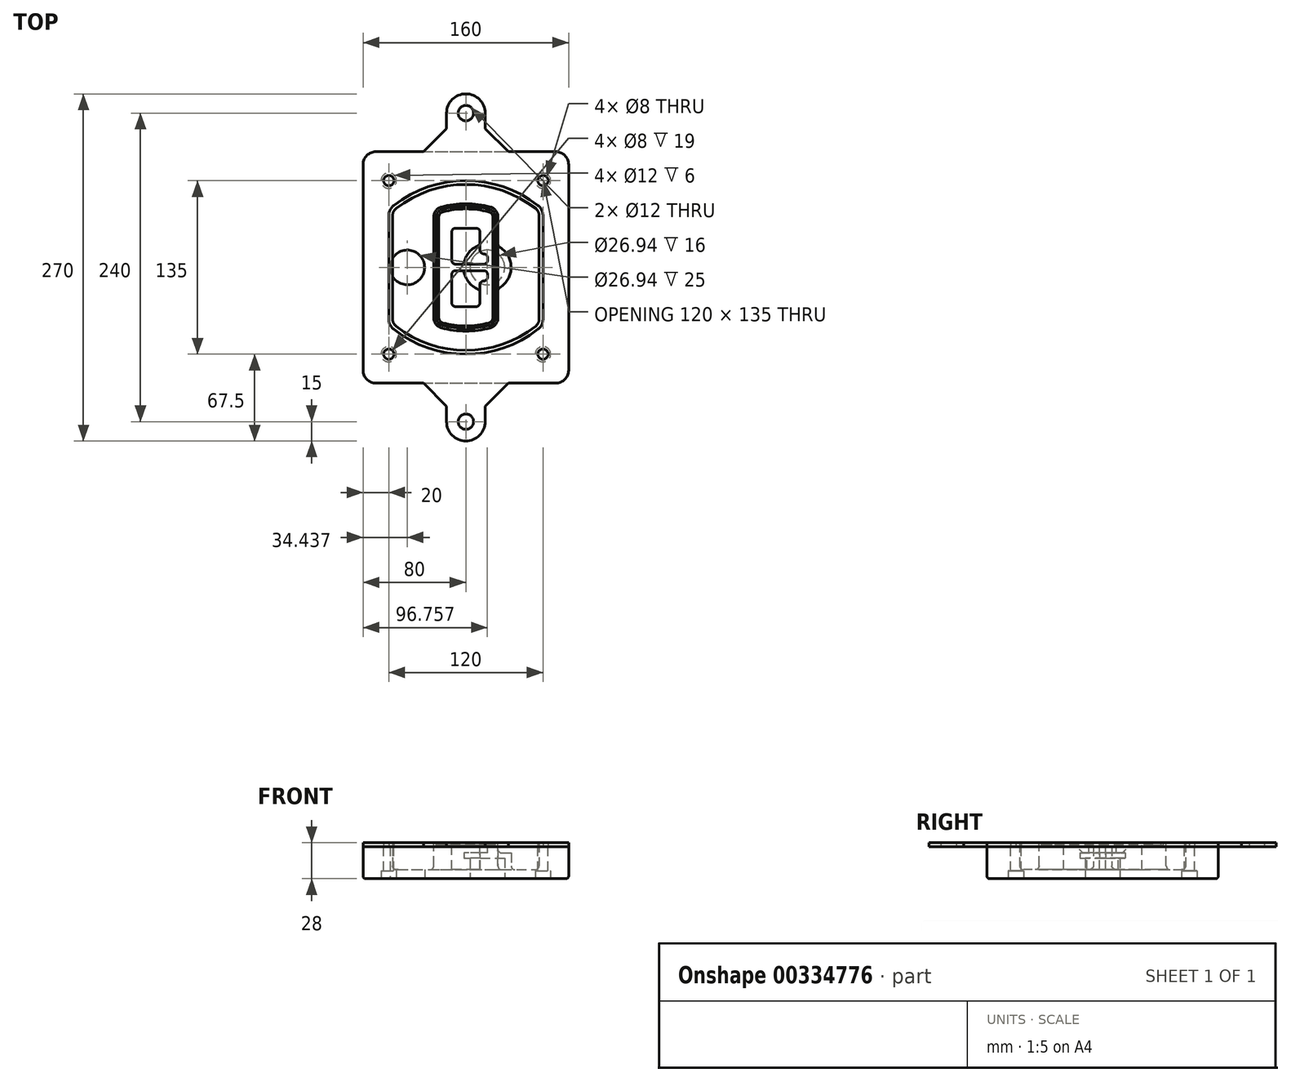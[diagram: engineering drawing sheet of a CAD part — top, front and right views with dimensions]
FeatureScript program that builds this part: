
annotation { "Feature Type Name" : "Feature", "Feature Type Description" : "" }
export const myFeature = defineFeature(function(context is Context, id is Id, definition is map)
    precondition{}
    {
        {
            var Q0;
            Q0=qCreatedBy(makeId("Top.planeOp"),FACE);
            var sketch = newSketch(context, id + "F0", { "sketchPlane" : qUnion([Q0])});
            skPoint(sketch, "E0.rect.middle", {"position": v(0, 0) * mm});
            skLineSegment(sketch, "E1.bottom", {"start": v(-70, -90) * mm, "end": v(70, -90) * mm});
            skLineSegment(sketch, "E1.top", {"start": v(-70, 90) * mm, "end": v(70, 90) * mm});
            skLineSegment(sketch, "E1.left", {"start": v(-80, -80) * mm, "end": v(-80, 80) * mm});
            skLineSegment(sketch, "E1.right", {"start": v(80, -80) * mm, "end": v(80, 80) * mm});
            skLineSegment(sketch, "E2", {"start": v(-80, 90) * mm, "end": v(80, -90) * mm, "construction": true});
            skLineSegment(sketch, "E3", {"start": v(80, 90) * mm, "end": v(-80, -90) * mm, "construction": true});
            skCircle(sketch, "E4", {"center": v(-60, 67.5) * mm, "radius": 4 * mm});
            skCircle(sketch, "E5", {"center": v(60, 67.5) * mm, "radius": 4 * mm});
            skCircle(sketch, "E6", {"center": v(60, -67.5) * mm, "radius": 4 * mm});
            skCircle(sketch, "E7", {"center": v(-60, -67.5) * mm, "radius": 4 * mm});
            skLineSegment(sketch, "E8", {"start": v(-60, 67.5) * mm, "end": v(60, 67.5) * mm, "construction": true});
            skLineSegment(sketch, "E9", {"start": v(60, 67.5) * mm, "end": v(60, -67.5) * mm, "construction": true});
            skLineSegment(sketch, "E10", {"start": v(60, -67.5) * mm, "end": v(-60, -67.5) * mm, "construction": true});
            skLineSegment(sketch, "E11", {"start": v(-60, -67.5) * mm, "end": v(-60, 67.5) * mm, "construction": true});
            skLineSegment(sketch, "E12", {"start": v(-60, 40.3) * mm, "end": v(-60, -40.3) * mm});
            skLineSegment(sketch, "E13", {"start": v(60, 40.3) * mm, "end": v(60, -40.3) * mm});
            skArc(sketch, "E14", {"start": v(56.15, 48.18) * mm, "mid": v(0, 67.5) * mm, "end": v(-56.15, 48.18) * mm});
            skArc(sketch, "E15", {"start": v(-56.15, -48.18) * mm, "mid": v(0, -67.5) * mm, "end": v(56.15, -48.18) * mm});
            skLineSegment(sketch, "E16", {"start": v(-60, 0) * mm, "end": v(60, 0) * mm, "construction": true});
            skPoint(sketch, "E17.visualSharp", {"position": v(-60, -45) * mm});
            skArc(sketch, "E17.filletArc", {"start": v(-60, -40.3) * mm, "mid": v(-58.99, -44.68) * mm, "end": v(-56.15, -48.18) * mm});
            skPoint(sketch, "E18.visualSharp", {"position": v(-60, 45) * mm});
            skArc(sketch, "E18.filletArc", {"start": v(-56.15, 48.18) * mm, "mid": v(-58.99, 44.68) * mm, "end": v(-60, 40.3) * mm});
            skPoint(sketch, "E19.visualSharp", {"position": v(60, 45) * mm});
            skArc(sketch, "E19.filletArc", {"start": v(60, 40.3) * mm, "mid": v(58.99, 44.68) * mm, "end": v(56.15, 48.18) * mm});
            skPoint(sketch, "E20.visualSharp", {"position": v(60, -45) * mm});
            skArc(sketch, "E20.filletArc", {"start": v(56.15, -48.18) * mm, "mid": v(58.99, -44.68) * mm, "end": v(60, -40.3) * mm});
            skPoint(sketch, "E21.visualSharp", {"position": v(-80, 90) * mm});
            skArc(sketch, "E21.filletArc", {"start": v(-70, 90) * mm, "mid": v(-77.07, 87.07) * mm, "end": v(-80, 80) * mm});
            skPoint(sketch, "E22.visualSharp", {"position": v(80, 90) * mm});
            skArc(sketch, "E22.filletArc", {"start": v(80, 80) * mm, "mid": v(77.07, 87.07) * mm, "end": v(70, 90) * mm});
            skPoint(sketch, "E23.visualSharp", {"position": v(80, -90) * mm});
            skArc(sketch, "E23.filletArc", {"start": v(70, -90) * mm, "mid": v(77.07, -87.07) * mm, "end": v(80, -80) * mm});
            skPoint(sketch, "E24.visualSharp", {"position": v(-80, -90) * mm});
            skArc(sketch, "E24.filletArc", {"start": v(-80, -80) * mm, "mid": v(-77.07, -87.07) * mm, "end": v(-70, -90) * mm});
            skArc(sketch, "E25.0", {"start": v(57, 40.3) * mm, "mid": v(56.3, 43.36) * mm, "end": v(54.3, 45.81) * mm});
            skLineSegment(sketch, "E25.1", {"start": v(57, 40.3) * mm, "end": v(57, -40.3) * mm});
            skArc(sketch, "E25.2", {"start": v(54.3, -45.81) * mm, "mid": v(56.3, -43.36) * mm, "end": v(57, -40.3) * mm});
            skArc(sketch, "E25.3", {"start": v(-54.3, -45.81) * mm, "mid": v(0, -64.5) * mm, "end": v(54.3, -45.81) * mm});
            skArc(sketch, "E25.4", {"start": v(-57, -40.3) * mm, "mid": v(-56.3, -43.36) * mm, "end": v(-54.3, -45.81) * mm});
            skArc(sketch, "E25.5", {"start": v(54.3, 45.81) * mm, "mid": v(0, 64.5) * mm, "end": v(-54.3, 45.81) * mm});
            skLineSegment(sketch, "E25.6", {"start": v(-57, 40.3) * mm, "end": v(-57, -40.3) * mm});
            skArc(sketch, "E25.7", {"start": v(-54.3, 45.81) * mm, "mid": v(-56.3, 43.36) * mm, "end": v(-57, 40.3) * mm});
            skArc(sketch, "E26.0", {"start": v(-58.62, 51.33) * mm, "mid": v(-62.58, 46.43) * mm, "end": v(-64, 40.3) * mm});
            skArc(sketch, "E26.1", {"start": v(58.62, 51.33) * mm, "mid": v(0, 71.5) * mm, "end": v(-58.62, 51.33) * mm});
            skArc(sketch, "E26.2", {"start": v(64, 40.3) * mm, "mid": v(62.58, 46.43) * mm, "end": v(58.62, 51.33) * mm});
            skLineSegment(sketch, "E26.3", {"start": v(64, 40.3) * mm, "end": v(64, -40.3) * mm});
            skArc(sketch, "E26.4", {"start": v(58.62, -51.33) * mm, "mid": v(62.58, -46.43) * mm, "end": v(64, -40.3) * mm});
            skLineSegment(sketch, "E26.5", {"start": v(-64, 40.3) * mm, "end": v(-64, -40.3) * mm});
            skArc(sketch, "E26.6", {"start": v(-58.62, -51.33) * mm, "mid": v(0, -71.5) * mm, "end": v(58.62, -51.33) * mm});
            skArc(sketch, "E26.7", {"start": v(-64, -40.3) * mm, "mid": v(-62.58, -46.43) * mm, "end": v(-58.62, -51.33) * mm});
            skSolve(sketch);
        }
        {
            var Q0;
            Q0=makeQuery(id+"F0.imprint","IMPRINT",FACE,{"disambiguationData":[TD([[makeQuery(id+"F0.imprint","IMPRINT",EDGE,{"derivedFrom":sQuery(id+"F0.wireOp",EDGE,"E1.bottom")}),1.0]])]});
            var Q1;
            Q1=makeQuery(id+"F0.imprint","IMPRINT",FACE,{"disambiguationData":[TD([[makeQuery(id+"F0.imprint","IMPRINT",EDGE,{"derivedFrom":sQuery(id+"F0.wireOp",EDGE,"E12")}),1.0]])]});
            var Q2;
            Q2=makeQuery(id+"F0.imprint","IMPRINT",FACE,{"disambiguationData":[TD([[makeQuery(id+"F0.imprint","IMPRINT",EDGE,{"derivedFrom":sQuery(id+"F0.wireOp",EDGE,"E25.0")}),1.0]])]});
            var Q3;
            Q3=makeQuery(id+"F0.imprint","IMPRINT",FACE,{"disambiguationData":[TD([[makeQuery(id+"F0.imprint","IMPRINT",EDGE,{"derivedFrom":sQuery(id+"F0.wireOp",EDGE,"E12")}),-1.0]])]});
            extrude(context, id + "F1", {"entities" : qUnion([Q0, Q1, Q2, Q3]), "oppositeDirection" : true, "depth" : 25 * mm});
        }
        {
            var Q0;
            Q0=makeQuery(id+"F0.imprint","IMPRINT",FACE,{"disambiguationData":[TD([[makeQuery(id+"F0.imprint","IMPRINT",EDGE,{"derivedFrom":sQuery(id+"F0.wireOp",EDGE,"E12")}),1.0]])]});
            extrude(context, id + "F2", {"entities" : qUnion([Q0]), "operationType" : NewBodyOperationType.ADD, "depth" : 3 * mm});
        }
        {
            var Q0;
            Q0=makeQuery(id+"F0.imprint","IMPRINT",FACE,{"disambiguationData":[TD([[makeQuery(id+"F0.imprint","IMPRINT",EDGE,{"derivedFrom":sQuery(id+"F0.wireOp",EDGE,"E25.0")}),1.0]])]});
            extrude(context, id + "F3", {"entities" : qUnion([Q0]), "operationType" : NewBodyOperationType.REMOVE, "oppositeDirection" : true, "depth" : 18 * mm});
        }
        {
            var Q0;
            Q0=makeQuery(id+"F2.opExtrude","CAP_FACE",FACE,{"disambiguationData":[OSD([sQuery(id+"F0.wireOp",EDGE,"E12"),sQuery(id+"F0.wireOp",EDGE,"E13"),sQuery(id+"F0.wireOp",EDGE,"E14"),sQuery(id+"F0.wireOp",EDGE,"E15"),sQuery(id+"F0.wireOp",EDGE,"E17.filletArc"),sQuery(id+"F0.wireOp",EDGE,"E18.filletArc"),sQuery(id+"F0.wireOp",EDGE,"E19.filletArc"),sQuery(id+"F0.wireOp",EDGE,"E20.filletArc"),sQuery(id+"F0.wireOp",EDGE,"E25.0"),sQuery(id+"F0.wireOp",EDGE,"E25.1"),sQuery(id+"F0.wireOp",EDGE,"E25.2"),sQuery(id+"F0.wireOp",EDGE,"E25.3"),sQuery(id+"F0.wireOp",EDGE,"E25.4"),sQuery(id+"F0.wireOp",EDGE,"E25.5"),sQuery(id+"F0.wireOp",EDGE,"E25.6"),sQuery(id+"F0.wireOp",EDGE,"E25.7")])],"isStart":false});
            var sketch = newSketch(context, id + "F4", { "sketchPlane" : qUnion([Q0])});
            skArc(sketch, "E27.0", {"start": v(-19.08, -46.97) * mm, "mid": v(0, -49.5) * mm, "end": v(19.08, -46.97) * mm});
            skArc(sketch, "E28.0", {"start": v(19.08, 46.97) * mm, "mid": v(0, 49.5) * mm, "end": v(-19.08, 46.97) * mm});
            skLineSegment(sketch, "E29", {"start": v(-25, 39.25) * mm, "end": v(-25, -39.25) * mm});
            skLineSegment(sketch, "E30", {"start": v(25, 39.25) * mm, "end": v(25, -39.25) * mm});
            skLineSegment(sketch, "E31", {"start": v(-25, 45.1) * mm, "end": v(25, 45.1) * mm, "construction": true});
            skLineSegment(sketch, "E32", {"start": v(-25, -45.1) * mm, "end": v(25, -45.1) * mm, "construction": true});
            skPoint(sketch, "E33.visualSharp", {"position": v(-25, 45.1) * mm});
            skArc(sketch, "E33.filletArc", {"start": v(-19.08, 46.97) * mm, "mid": v(-23.35, 44.11) * mm, "end": v(-25, 39.25) * mm});
            skPoint(sketch, "E34.visualSharp", {"position": v(25, 45.1) * mm});
            skArc(sketch, "E34.filletArc", {"start": v(25, 39.25) * mm, "mid": v(23.35, 44.11) * mm, "end": v(19.08, 46.97) * mm});
            skPoint(sketch, "E35.visualSharp", {"position": v(25, -45.1) * mm});
            skArc(sketch, "E35.filletArc", {"start": v(19.08, -46.97) * mm, "mid": v(23.35, -44.11) * mm, "end": v(25, -39.25) * mm});
            skPoint(sketch, "E36.visualSharp", {"position": v(-25, -45.1) * mm});
            skArc(sketch, "E36.filletArc", {"start": v(-25, -39.25) * mm, "mid": v(-23.35, -44.11) * mm, "end": v(-19.08, -46.97) * mm});
            skArc(sketch, "E37.0", {"start": v(54.3, 45.81) * mm, "mid": v(0, 64.5) * mm, "end": v(-54.3, 45.81) * mm});
            skArc(sketch, "E37.1", {"start": v(-54.3, 45.81) * mm, "mid": v(-56.3, 43.36) * mm, "end": v(-57, 40.3) * mm});
            skLineSegment(sketch, "E37.2", {"start": v(-57, 40.3) * mm, "end": v(-57, -40.3) * mm});
            skArc(sketch, "E37.3", {"start": v(-57, -40.3) * mm, "mid": v(-56.3, -43.36) * mm, "end": v(-54.3, -45.81) * mm});
            skArc(sketch, "E37.4", {"start": v(-54.3, -45.81) * mm, "mid": v(0, -64.5) * mm, "end": v(54.3, -45.81) * mm});
            skArc(sketch, "E37.5", {"start": v(54.3, -45.81) * mm, "mid": v(56.3, -43.36) * mm, "end": v(57, -40.3) * mm});
            skLineSegment(sketch, "E37.6", {"start": v(57, 40.3) * mm, "end": v(57, -40.3) * mm});
            skArc(sketch, "E37.7", {"start": v(57, 40.3) * mm, "mid": v(56.3, 43.36) * mm, "end": v(54.3, 45.81) * mm});
            skLineSegment(sketch, "E38.0", {"start": v(23, 39.25) * mm, "end": v(23, -39.25) * mm});
            skArc(sketch, "E38.1", {"start": v(18.56, -45.04) * mm, "mid": v(21.76, -42.9) * mm, "end": v(23, -39.25) * mm});
            skArc(sketch, "E38.2", {"start": v(-18.56, -45.04) * mm, "mid": v(0, -47.5) * mm, "end": v(18.56, -45.04) * mm});
            skArc(sketch, "E38.3", {"start": v(-23, -39.25) * mm, "mid": v(-21.76, -42.9) * mm, "end": v(-18.56, -45.04) * mm});
            skLineSegment(sketch, "E38.4", {"start": v(-23, 39.25) * mm, "end": v(-23, -39.25) * mm});
            skArc(sketch, "E38.5", {"start": v(23, 39.25) * mm, "mid": v(21.76, 42.9) * mm, "end": v(18.56, 45.04) * mm});
            skArc(sketch, "E38.6", {"start": v(-18.56, 45.04) * mm, "mid": v(-21.76, 42.9) * mm, "end": v(-23, 39.25) * mm});
            skArc(sketch, "E38.7", {"start": v(18.56, 45.04) * mm, "mid": v(0, 47.5) * mm, "end": v(-18.56, 45.04) * mm});
            skArc(sketch, "E39.0", {"start": v(21, 39.25) * mm, "mid": v(20.18, 41.68) * mm, "end": v(18.04, 43.1) * mm});
            skLineSegment(sketch, "E39.1", {"start": v(21, 39.25) * mm, "end": v(21, -39.25) * mm});
            skArc(sketch, "E39.2", {"start": v(18.04, -43.1) * mm, "mid": v(20.18, -41.68) * mm, "end": v(21, -39.25) * mm});
            skArc(sketch, "E39.3", {"start": v(-18.04, -43.1) * mm, "mid": v(0, -45.5) * mm, "end": v(18.04, -43.1) * mm});
            skArc(sketch, "E39.4", {"start": v(-21, -39.25) * mm, "mid": v(-20.18, -41.68) * mm, "end": v(-18.04, -43.1) * mm});
            skArc(sketch, "E39.5", {"start": v(18.04, 43.1) * mm, "mid": v(0, 45.5) * mm, "end": v(-18.04, 43.1) * mm});
            skLineSegment(sketch, "E39.6", {"start": v(-21, 39.25) * mm, "end": v(-21, -39.25) * mm});
            skArc(sketch, "E39.7", {"start": v(-18.04, 43.1) * mm, "mid": v(-20.18, 41.68) * mm, "end": v(-21, 39.25) * mm});
            skLineSegment(sketch, "E40", {"start": v(-25, 0) * mm, "end": v(25, 0) * mm, "construction": true});
            skLineSegment(sketch, "E41", {"start": v(-11, 5.5) * mm, "end": v(-11, 27.5) * mm});
            skLineSegment(sketch, "E42", {"start": v(-8, 30.5) * mm, "end": v(8, 30.5) * mm});
            skLineSegment(sketch, "E43", {"start": v(11, 27.5) * mm, "end": v(11, 13.5) * mm});
            skLineSegment(sketch, "E44", {"start": v(14, 10.5) * mm, "end": v(14, 10.5) * mm});
            skLineSegment(sketch, "E45", {"start": v(17, 7.5) * mm, "end": v(17, 5.5) * mm});
            skLineSegment(sketch, "E46", {"start": v(14, 2.5) * mm, "end": v(-8, 2.5) * mm});
            skPoint(sketch, "E47.visualSharp", {"position": v(-11, 30.5) * mm});
            skArc(sketch, "E47.filletArc", {"start": v(-8, 30.5) * mm, "mid": v(-10.12, 29.62) * mm, "end": v(-11, 27.5) * mm});
            skPoint(sketch, "E48.visualSharp", {"position": v(11, 30.5) * mm});
            skArc(sketch, "E48.filletArc", {"start": v(11, 27.5) * mm, "mid": v(10.12, 29.62) * mm, "end": v(8, 30.5) * mm});
            skPoint(sketch, "E49.visualSharp", {"position": v(11, 10.5) * mm});
            skArc(sketch, "E49.filletArc", {"start": v(11, 13.5) * mm, "mid": v(11.88, 11.38) * mm, "end": v(14, 10.5) * mm});
            skPoint(sketch, "E50.visualSharp", {"position": v(17, 10.5) * mm});
            skArc(sketch, "E50.filletArc", {"start": v(17, 7.5) * mm, "mid": v(16.12, 9.62) * mm, "end": v(14, 10.5) * mm});
            skPoint(sketch, "E51.visualSharp", {"position": v(17, 2.5) * mm});
            skArc(sketch, "E51.filletArc", {"start": v(14, 2.5) * mm, "mid": v(16.12, 3.38) * mm, "end": v(17, 5.5) * mm});
            skPoint(sketch, "E52.visualSharp", {"position": v(-11, 2.5) * mm});
            skArc(sketch, "E52.filletArc", {"start": v(-11, 5.5) * mm, "mid": v(-10.12, 3.38) * mm, "end": v(-8, 2.5) * mm});
            skLineSegment(sketch, "E53.0.MirrorCS", {"start": v(14, -2.5) * mm, "end": v(-8, -2.5) * mm});
            skArc(sketch, "E54.0.MirrorCS", {"start": v(-11, -5.5) * mm, "mid": v(-10.12, -3.38) * mm, "end": v(-8, -2.5) * mm});
            skLineSegment(sketch, "E55.0.MirrorCS", {"start": v(-11, -5.5) * mm, "end": v(-11, -27.5) * mm});
            skArc(sketch, "E56.0.MirrorCS", {"start": v(-8, -30.5) * mm, "mid": v(-10.12, -29.62) * mm, "end": v(-11, -27.5) * mm});
            skLineSegment(sketch, "E57.0.MirrorCS", {"start": v(-8, -30.5) * mm, "end": v(8, -30.5) * mm});
            skArc(sketch, "E58.0.MirrorCS", {"start": v(11, -27.5) * mm, "mid": v(10.12, -29.62) * mm, "end": v(8, -30.5) * mm});
            skLineSegment(sketch, "E59.0.MirrorCS", {"start": v(11, -27.5) * mm, "end": v(11, -13.5) * mm});
            skArc(sketch, "E60.0.MirrorCS", {"start": v(11, -13.5) * mm, "mid": v(11.88, -11.38) * mm, "end": v(14, -10.5) * mm});
            skArc(sketch, "E61.0.MirrorCS", {"start": v(17, -7.5) * mm, "mid": v(16.12, -9.62) * mm, "end": v(14, -10.5) * mm});
            skLineSegment(sketch, "E62.0.MirrorCS", {"start": v(17, -7.5) * mm, "end": v(17, -5.5) * mm});
            skArc(sketch, "E63.0.MirrorCS", {"start": v(14, -2.5) * mm, "mid": v(16.12, -3.38) * mm, "end": v(17, -5.5) * mm});
            skSolve(sketch);
        }
        {
            var Q0;
            Q0=makeQuery(id+"F4.imprint","IMPRINT",FACE,{"disambiguationData":[TD([[makeQuery(id+"F4.imprint","IMPRINT",EDGE,{"derivedFrom":sQuery(id+"F4.wireOp",EDGE,"E27.0")}),1.0]])]});
            var Q1;
            Q1=makeQuery(id+"F4.imprint","IMPRINT",FACE,{"disambiguationData":[TD([[makeQuery(id+"F4.imprint","IMPRINT",EDGE,{"derivedFrom":sQuery(id+"F4.wireOp",EDGE,"E38.0")}),-1.0]])]});
            var Q2;
            Q2=makeQuery(id+"F4.imprint","IMPRINT",FACE,{"disambiguationData":[TD([[makeQuery(id+"F4.imprint","IMPRINT",EDGE,{"derivedFrom":sQuery(id+"F4.wireOp",EDGE,"E39.0")}),1.0]])]});
            extrude(context, id + "F5", {"entities" : qUnion([Q0, Q1, Q2]), "operationType" : NewBodyOperationType.ADD, "endBound" : BoundingType.UP_TO_NEXT, "oppositeDirection" : true, "depth" : 25 * mm});
        }
        {
            var Q0;
            Q0=makeQuery(id+"F4.imprint","IMPRINT",FACE,{"disambiguationData":[TD([[makeQuery(id+"F4.imprint","IMPRINT",EDGE,{"derivedFrom":sQuery(id+"F4.wireOp",EDGE,"E38.0")}),-1.0]])]});
            extrude(context, id + "F6", {"entities" : qUnion([Q0]), "operationType" : NewBodyOperationType.REMOVE, "oppositeDirection" : true, "depth" : 2 * mm});
        }
        {
            var Q0;
            Q0=makeQuery(id+"F1.opExtrude","CAP_FACE",FACE,{"disambiguationData":[OSD([sQuery(id+"F0.wireOp",EDGE,"E1.bottom"),sQuery(id+"F0.wireOp",EDGE,"E1.top"),sQuery(id+"F0.wireOp",EDGE,"E1.left"),sQuery(id+"F0.wireOp",EDGE,"E1.right"),sQuery(id+"F0.wireOp",EDGE,"E4"),sQuery(id+"F0.wireOp",EDGE,"E5"),sQuery(id+"F0.wireOp",EDGE,"E6"),sQuery(id+"F0.wireOp",EDGE,"E7"),sQuery(id+"F0.wireOp",EDGE,"E21.filletArc"),sQuery(id+"F0.wireOp",EDGE,"E22.filletArc"),sQuery(id+"F0.wireOp",EDGE,"E23.filletArc"),sQuery(id+"F0.wireOp",EDGE,"E24.filletArc")])],"isStart":false});
            var sketch = newSketch(context, id + "F7", { "sketchPlane" : qUnion([Q0])});
            skCircle(sketch, "E64", {"center": v(16.76, 0) * mm, "radius": 13.47 * mm});
            skCircle(sketch, "E65", {"center": v(-45.56, 0) * mm, "radius": 13.47 * mm});
            skLineSegment(sketch, "E66", {"start": v(80, 0) * mm, "end": v(-80, 0) * mm});
            skCircle(sketch, "E67", {"center": v(16.76, 0) * mm, "radius": 18.47 * mm});
            skCircle(sketch, "E68", {"center": v(60, -67.5) * mm, "radius": 6 * mm});
            skCircle(sketch, "E69", {"center": v(-60, -67.5) * mm, "radius": 6 * mm});
            skCircle(sketch, "E70", {"center": v(-60, 67.5) * mm, "radius": 6 * mm});
            skCircle(sketch, "E71", {"center": v(60, 67.5) * mm, "radius": 6 * mm});
            skSolve(sketch);
        }
        {
            var Q0;
            {var subQ1=sQuery(id+"F7.wireOp",EDGE,"E66");var subQ4=sQuery(id+"F7.wireOp",EDGE,"E64");var subQ6=makeQuery(id+"F7.imprint","INTERSECT",VERTEX,{"disambiguationData":[OD(0.0)],"derivedFrom":[subQ4,subQ1]});Q0=makeQuery(id+"F7.imprint","IMPRINT",FACE,{"disambiguationData":[TD([[makeQuery(id+"F7.imprint","IMPRINT",EDGE,{"disambiguationData":[TD([[subQ6,-1.0]])],"derivedFrom":subQ4}),-1.0]])]});}
            var Q1;
            {var subQ0=sQuery(id+"F7.wireOp",EDGE,"E66");var subQ1=sQuery(id+"F7.wireOp",EDGE,"E64");var subQ3=makeQuery(id+"F7.imprint","INTERSECT",VERTEX,{"disambiguationData":[OD(0.0)],"derivedFrom":[subQ1,subQ0]});Q1=makeQuery(id+"F7.imprint","IMPRINT",FACE,{"disambiguationData":[TD([[makeQuery(id+"F7.imprint","IMPRINT",EDGE,{"disambiguationData":[TD([[subQ3,-1.0]])],"derivedFrom":subQ1}),1.0]])]});}
            var Q2;
            {var subQ0=sQuery(id+"F7.wireOp",EDGE,"E66");var subQ1=sQuery(id+"F7.wireOp",EDGE,"E64");var subQ3=makeQuery(id+"F7.imprint","INTERSECT",VERTEX,{"disambiguationData":[OD(0.0)],"derivedFrom":[subQ1,subQ0]});Q2=makeQuery(id+"F7.imprint","IMPRINT",FACE,{"disambiguationData":[TD([[makeQuery(id+"F7.imprint","IMPRINT",EDGE,{"disambiguationData":[TD([[subQ3,1.0]])],"derivedFrom":subQ1}),1.0]])]});}
            var Q3;
            {var subQ1=sQuery(id+"F7.wireOp",EDGE,"E66");var subQ4=sQuery(id+"F7.wireOp",EDGE,"E64");var subQ6=makeQuery(id+"F7.imprint","INTERSECT",VERTEX,{"disambiguationData":[OD(0.0)],"derivedFrom":[subQ4,subQ1]});Q3=makeQuery(id+"F7.imprint","IMPRINT",FACE,{"disambiguationData":[TD([[makeQuery(id+"F7.imprint","IMPRINT",EDGE,{"disambiguationData":[TD([[subQ6,1.0]])],"derivedFrom":subQ4}),-1.0]])]});}
            extrude(context, id + "F8", {"entities" : qUnion([Q0, Q1, Q2, Q3]), "operationType" : NewBodyOperationType.ADD, "oppositeDirection" : true, "depth" : 20 * mm});
        }
        {
            var Q0;
            {var subQ0=sQuery(id+"F7.wireOp",EDGE,"E66");var subQ1=sQuery(id+"F7.wireOp",EDGE,"E64");var subQ3=makeQuery(id+"F7.imprint","INTERSECT",VERTEX,{"disambiguationData":[OD(0.0)],"derivedFrom":[subQ1,subQ0]});Q0=makeQuery(id+"F7.imprint","IMPRINT",FACE,{"disambiguationData":[TD([[makeQuery(id+"F7.imprint","IMPRINT",EDGE,{"disambiguationData":[TD([[subQ3,-1.0]])],"derivedFrom":subQ1}),1.0]])]});}
            var Q1;
            {var subQ0=sQuery(id+"F7.wireOp",EDGE,"E66");var subQ1=sQuery(id+"F7.wireOp",EDGE,"E64");var subQ3=makeQuery(id+"F7.imprint","INTERSECT",VERTEX,{"disambiguationData":[OD(0.0)],"derivedFrom":[subQ1,subQ0]});Q1=makeQuery(id+"F7.imprint","IMPRINT",FACE,{"disambiguationData":[TD([[makeQuery(id+"F7.imprint","IMPRINT",EDGE,{"disambiguationData":[TD([[subQ3,1.0]])],"derivedFrom":subQ1}),1.0]])]});}
            extrude(context, id + "F9", {"entities" : qUnion([Q0, Q1]), "operationType" : NewBodyOperationType.REMOVE, "oppositeDirection" : true, "depth" : 16 * mm});
        }
        {
            var Q0;
            {var subQ0=sQuery(id+"F7.wireOp",EDGE,"E66");var subQ1=sQuery(id+"F7.wireOp",EDGE,"E65");var subQ3=makeQuery(id+"F7.imprint","INTERSECT",VERTEX,{"disambiguationData":[OD(0.0)],"derivedFrom":[subQ1,subQ0]});Q0=makeQuery(id+"F7.imprint","IMPRINT",FACE,{"disambiguationData":[TD([[makeQuery(id+"F7.imprint","IMPRINT",EDGE,{"disambiguationData":[TD([[subQ3,-1.0]])],"derivedFrom":subQ1}),1.0]])]});}
            var Q1;
            {var subQ0=sQuery(id+"F7.wireOp",EDGE,"E66");var subQ1=sQuery(id+"F7.wireOp",EDGE,"E65");var subQ3=makeQuery(id+"F7.imprint","INTERSECT",VERTEX,{"disambiguationData":[OD(0.0)],"derivedFrom":[subQ1,subQ0]});Q1=makeQuery(id+"F7.imprint","IMPRINT",FACE,{"disambiguationData":[TD([[makeQuery(id+"F7.imprint","IMPRINT",EDGE,{"disambiguationData":[TD([[subQ3,1.0]])],"derivedFrom":subQ1}),1.0]])]});}
            extrude(context, id + "F10", {"entities" : qUnion([Q0, Q1]), "operationType" : NewBodyOperationType.REMOVE, "oppositeDirection" : true, "depth" : 25 * mm});
        }
        {
            var Q0;
            Q0=makeQuery(id+"F7.imprint","IMPRINT",FACE,{"disambiguationData":[TD([[makeQuery(id+"F7.imprint","IMPRINT",EDGE,{"derivedFrom":sQuery(id+"F7.wireOp",EDGE,"E68")}),1.0]])]});
            var Q1;
            Q1=makeQuery(id+"F7.imprint","IMPRINT",FACE,{"disambiguationData":[TD([[makeQuery(id+"F7.imprint","IMPRINT",EDGE,{"derivedFrom":makeQuery(id+"F1.opExtrude","CAP_EDGE",EDGE,{"disambiguationData":[OSD([sQuery(id+"F0.wireOp",EDGE,"E5")])],"isStart":false})}),-1.0]])]});
            var Q2;
            Q2=makeQuery(id+"F7.imprint","IMPRINT",FACE,{"disambiguationData":[TD([[makeQuery(id+"F7.imprint","IMPRINT",EDGE,{"derivedFrom":sQuery(id+"F7.wireOp",EDGE,"E69")}),1.0]])]});
            var Q3;
            Q3=makeQuery(id+"F7.imprint","IMPRINT",FACE,{"disambiguationData":[TD([[makeQuery(id+"F7.imprint","IMPRINT",EDGE,{"derivedFrom":makeQuery(id+"F1.opExtrude","CAP_EDGE",EDGE,{"disambiguationData":[OSD([sQuery(id+"F0.wireOp",EDGE,"E4")])],"isStart":false})}),-1.0]])]});
            var Q4;
            Q4=makeQuery(id+"F7.imprint","IMPRINT",FACE,{"disambiguationData":[TD([[makeQuery(id+"F7.imprint","IMPRINT",EDGE,{"derivedFrom":sQuery(id+"F7.wireOp",EDGE,"E70")}),1.0]])]});
            var Q5;
            Q5=makeQuery(id+"F7.imprint","IMPRINT",FACE,{"disambiguationData":[TD([[makeQuery(id+"F7.imprint","IMPRINT",EDGE,{"derivedFrom":makeQuery(id+"F1.opExtrude","CAP_EDGE",EDGE,{"disambiguationData":[OSD([sQuery(id+"F0.wireOp",EDGE,"E7")])],"isStart":false})}),-1.0]])]});
            var Q6;
            Q6=makeQuery(id+"F7.imprint","IMPRINT",FACE,{"disambiguationData":[TD([[makeQuery(id+"F7.imprint","IMPRINT",EDGE,{"derivedFrom":sQuery(id+"F7.wireOp",EDGE,"E71")}),1.0]])]});
            var Q7;
            Q7=makeQuery(id+"F7.imprint","IMPRINT",FACE,{"disambiguationData":[TD([[makeQuery(id+"F7.imprint","IMPRINT",EDGE,{"derivedFrom":makeQuery(id+"F1.opExtrude","CAP_EDGE",EDGE,{"disambiguationData":[OSD([sQuery(id+"F0.wireOp",EDGE,"E6")])],"isStart":false})}),-1.0]])]});
            extrude(context, id + "F11", {"entities" : qUnion([Q0, Q1, Q2, Q3, Q4, Q5, Q6, Q7]), "operationType" : NewBodyOperationType.REMOVE, "oppositeDirection" : true, "depth" : 6 * mm});
        }
        {
            var Q0;
            Q0=makeQuery(id+"F9.boolean.opBoolean","COPY",FACE,{"derivedFrom":makeQuery(id+"F9.opExtrude","CAP_FACE",FACE,{"disambiguationData":[OSD([sQuery(id+"F7.wireOp",EDGE,"E64")])],"isStart":false})});
            var sketch = newSketch(context, id + "F12", { "sketchPlane" : qUnion([Q0])});
            skArc(sketch, "E72.0", {"start": v(11, 17.55) * mm, "mid": v(2.57, 11.82) * mm, "end": v(-1.54, 2.5) * mm});
            skArc(sketch, "E72.1", {"start": v(-1.54, -2.5) * mm, "mid": v(2.57, -11.82) * mm, "end": v(11, -17.55) * mm});
            skLineSegment(sketch, "E73", {"start": v(-1.54, -2.5) * mm, "end": v(14, -2.5) * mm});
            skLineSegment(sketch, "E74.0", {"start": v(14, 2.5) * mm, "end": v(-1.54, 2.5) * mm});
            skArc(sketch, "E74.1", {"start": v(14, 2.5) * mm, "mid": v(16.12, 3.38) * mm, "end": v(17, 5.5) * mm});
            skLineSegment(sketch, "E74.2", {"start": v(17, 7.5) * mm, "end": v(17, 5.5) * mm});
            skArc(sketch, "E74.3", {"start": v(17, 7.5) * mm, "mid": v(16.12, 9.62) * mm, "end": v(14, 10.5) * mm});
            skArc(sketch, "E74.4", {"start": v(11, 13.5) * mm, "mid": v(11.88, 11.38) * mm, "end": v(14, 10.5) * mm});
            skLineSegment(sketch, "E74.5", {"start": v(11, 17.55) * mm, "end": v(11, 13.5) * mm});
            skLineSegment(sketch, "E74.7", {"start": v(14, -2.5) * mm, "end": v(-1.54, -2.5) * mm});
            skArc(sketch, "E74.8", {"start": v(14, -2.5) * mm, "mid": v(16.12, -3.38) * mm, "end": v(17, -5.5) * mm});
            skLineSegment(sketch, "E74.9", {"start": v(17, -7.5) * mm, "end": v(17, -5.5) * mm});
            skArc(sketch, "E74.10", {"start": v(17, -7.5) * mm, "mid": v(16.12, -9.62) * mm, "end": v(14, -10.5) * mm});
            skArc(sketch, "E74.11", {"start": v(11, -13.5) * mm, "mid": v(11.88, -11.38) * mm, "end": v(14, -10.5) * mm});
            skLineSegment(sketch, "E74.12", {"start": v(11, -17.55) * mm, "end": v(11, -13.5) * mm});
            skPoint(sketch, "E75.orphan", {"position": v(11, -27.5) * mm});
            skPoint(sketch, "E76.orphan", {"position": v(-8, -2.5) * mm});
            skPoint(sketch, "E77.orphan", {"position": v(-8, 2.5) * mm});
            skPoint(sketch, "E78.orphan", {"position": v(11, 27.5) * mm});
            skSolve(sketch);
        }
        {
            var Q0;
            {var subQ7=sQuery(id+"F12.wireOp",EDGE,"E72.0");var subQ14=sQuery(id+"F12.wireOp",EDGE,"E72.1");var subQ16=sQuery(id+"F12.wireOp",EDGE,"E74.1");var subQ18=sQuery(id+"F12.wireOp",EDGE,"E74.8");Q0=qUnion([makeQuery(id+"F12.imprint","IMPRINT",FACE,{"disambiguationData":[TD([[makeQuery(id+"F12.imprint","IMPRINT",EDGE,{"derivedFrom":subQ7}),1.0]])]}),makeQuery(id+"F12.imprint","IMPRINT",FACE,{"disambiguationData":[TD([[makeQuery(id+"F12.imprint","IMPRINT",EDGE,{"derivedFrom":subQ14}),1.0]])]}),makeQuery(id+"F12.imprint","IMPRINT",FACE,{"disambiguationData":[TD([[makeQuery(id+"F12.imprint","IMPRINT",EDGE,{"derivedFrom":subQ16}),1.0]])]}),makeQuery(id+"F12.imprint","IMPRINT",FACE,{"disambiguationData":[TD([[makeQuery(id+"F12.imprint","IMPRINT",EDGE,{"derivedFrom":subQ18}),-1.0]])]})]);}
            var Q1;
            Q1=makeQuery(id+"F5.boolean.opBoolean","SPLIT",FACE,{"disambiguationData":[TD([makeQuery(id+"F5.opExtrude","SWEPT_FACE",FACE,{"disambiguationData":[OSD([sQuery(id+"F4.wireOp",EDGE,"E41")])]})])],"derivedFrom":makeQuery(id+"F3.boolean.opBoolean","COPY",FACE,{"derivedFrom":makeQuery(id+"F3.opExtrude","CAP_FACE",FACE,{"disambiguationData":[OSD([sQuery(id+"F0.wireOp",EDGE,"E25.0"),sQuery(id+"F0.wireOp",EDGE,"E25.1"),sQuery(id+"F0.wireOp",EDGE,"E25.2"),sQuery(id+"F0.wireOp",EDGE,"E25.3"),sQuery(id+"F0.wireOp",EDGE,"E25.4"),sQuery(id+"F0.wireOp",EDGE,"E25.5"),sQuery(id+"F0.wireOp",EDGE,"E25.6"),sQuery(id+"F0.wireOp",EDGE,"E25.7")])],"isStart":false})})});
            extrude(context, id + "F13", {"entities" : qUnion([Q0]), "operationType" : NewBodyOperationType.REMOVE, "endBound" : BoundingType.UP_TO_SURFACE, "endBoundEntityFace" : qUnion([Q1]), "depth" : 25 * mm});
        }
        {
            var Q0;
            Q0=makeQuery(id+"F3.boolean.opBoolean","COPY",EDGE,{"derivedFrom":makeQuery(id+"F3.opExtrude","CAP_EDGE",EDGE,{"disambiguationData":[OSD([sQuery(id+"F0.wireOp",EDGE,"E25.6")])],"isStart":false})});
            var Q1;
            Q1=makeQuery(id+"F8.boolean.opBoolean","INTERSECT",EDGE,{"derivedFrom":[makeQuery(id+"F5.opExtrude","SWEPT_FACE",FACE,{"disambiguationData":[OSD([sQuery(id+"F4.wireOp",EDGE,"E30")])]}),makeQuery(id+"F8.opExtrude","CAP_FACE",FACE,{"disambiguationData":[OSD([sQuery(id+"F7.wireOp",EDGE,"E67")])],"isStart":false})]});
            var Q2;
            Q2=makeQuery(id+"F8.boolean.opBoolean","INTERSECT",EDGE,{"disambiguationData":[OD(1.0)],"derivedFrom":[makeQuery(id+"F5.opExtrude","SWEPT_FACE",FACE,{"disambiguationData":[OSD([sQuery(id+"F4.wireOp",EDGE,"E30")])]}),makeQuery(id+"F8.opExtrude","SWEPT_FACE",FACE,{"disambiguationData":[OSD([sQuery(id+"F7.wireOp",EDGE,"E67")])]})]});
            var Q3;
            {var subQ0=sQuery(id+"F4.wireOp",EDGE,"E30");Q3=makeQuery(id+"F8.boolean.opBoolean","SPLIT",EDGE,{"disambiguationData":[TD([makeQuery(id+"F5.opExtrude","SWEPT_FACE",FACE,{"disambiguationData":[OSD([sQuery(id+"F4.wireOp",EDGE,"E35.filletArc")])]})])],"derivedFrom":makeQuery(id+"F5.opExtrude","CAP_EDGE",EDGE,{"disambiguationData":[OSD([subQ0])],"isStart":false})});}
            var Q4;
            {var subQ0=sQuery(id+"F0.wireOp",EDGE,"E25.7");var subQ1=sQuery(id+"F0.wireOp",EDGE,"E25.1");var subQ2=sQuery(id+"F0.wireOp",EDGE,"E25.6");var subQ3=sQuery(id+"F0.wireOp",EDGE,"E25.5");var subQ4=sQuery(id+"F0.wireOp",EDGE,"E25.4");var subQ5=sQuery(id+"F0.wireOp",EDGE,"E25.0");var subQ6=sQuery(id+"F0.wireOp",EDGE,"E25.2");var subQ7=sQuery(id+"F0.wireOp",EDGE,"E25.3");Q4=makeQuery(id+"F8.boolean.opBoolean","INTERSECT",EDGE,{"derivedFrom":[makeQuery(id+"F5.boolean.opBoolean","SPLIT",FACE,{"disambiguationData":[TD([makeQuery(id+"F2.opExtrude","SWEPT_FACE",FACE,{"disambiguationData":[OSD([subQ5])]})])],"derivedFrom":makeQuery(id+"F3.boolean.opBoolean","COPY",FACE,{"derivedFrom":makeQuery(id+"F3.opExtrude","CAP_FACE",FACE,{"disambiguationData":[OSD([subQ5,subQ1,subQ6,subQ7,subQ4,subQ3,subQ2,subQ0])],"isStart":false})})}),makeQuery(id+"F8.opExtrude","SWEPT_FACE",FACE,{"disambiguationData":[OSD([sQuery(id+"F7.wireOp",EDGE,"E67")])]})]});}
            var Q5;
            Q5=makeQuery(id+"F8.boolean.opBoolean","INTERSECT",EDGE,{"disambiguationData":[OD(0.0)],"derivedFrom":[makeQuery(id+"F5.opExtrude","SWEPT_FACE",FACE,{"disambiguationData":[OSD([sQuery(id+"F4.wireOp",EDGE,"E30")])]}),makeQuery(id+"F8.opExtrude","SWEPT_FACE",FACE,{"disambiguationData":[OSD([sQuery(id+"F7.wireOp",EDGE,"E67")])]})]});
            fillet(context, id + "F14", {"entities" : qUnion([Q0, Q1, Q2, Q3, Q4, Q5]), "radius" : 3 * mm, "tangentPropagation" : true, "allowEdgeOverflow" : false});
        }
        {
            var Q0;
            Q0=makeQuery(id+"F1.opExtrude","CAP_EDGE",EDGE,{"disambiguationData":[OSD([sQuery(id+"F0.wireOp",EDGE,"E1.bottom")])],"isStart":false});
            fillet(context, id + "F15", {"entities" : qUnion([Q0]), "radius" : 2 * mm, "tangentPropagation" : true, "allowEdgeOverflow" : false});
        }
        {
            var Q0;
            {var subQ0=sQuery(id+"F0.wireOp",EDGE,"E21.filletArc");var subQ1=sQuery(id+"F0.wireOp",EDGE,"E7");var subQ2=sQuery(id+"F0.wireOp",EDGE,"E6");var subQ3=sQuery(id+"F0.wireOp",EDGE,"E5");var subQ4=sQuery(id+"F0.wireOp",EDGE,"E4");var subQ5=sQuery(id+"F0.wireOp",EDGE,"E22.filletArc");var subQ6=sQuery(id+"F0.wireOp",EDGE,"E1.bottom");var subQ7=sQuery(id+"F0.wireOp",EDGE,"E1.right");var subQ8=sQuery(id+"F0.wireOp",EDGE,"E1.top");var subQ9=sQuery(id+"F0.wireOp",EDGE,"E1.left");var subQ10=sQuery(id+"F0.wireOp",EDGE,"E23.filletArc");var subQ11=sQuery(id+"F0.wireOp",EDGE,"E24.filletArc");Q0=makeQuery(id+"F2.boolean.opBoolean","SPLIT",FACE,{"disambiguationData":[TD([makeQuery(id+"F1.opExtrude","SWEPT_FACE",FACE,{"disambiguationData":[OSD([subQ6])]})])],"derivedFrom":makeQuery(id+"F1.opExtrude","CAP_FACE",FACE,{"disambiguationData":[OSD([subQ6,subQ8,subQ9,subQ7,subQ4,subQ3,subQ2,subQ1,subQ0,subQ5,subQ10,subQ11])],"isStart":true})});}
            var sketch = newSketch(context, id + "F16", { "sketchPlane" : qUnion([Q0])});
            skLineSegment(sketch, "E79", {"start": v(0, 90) * mm, "end": v(0, 120) * mm, "construction": true});
            skPoint(sketch, "E79.endSnap0", {"position": v(0, 90) * mm});
            skCircle(sketch, "E80", {"center": v(0, 120) * mm, "radius": 6 * mm});
            skLineSegment(sketch, "E81", {"start": v(-33, 90) * mm, "end": v(-15, 108) * mm});
            skLineSegment(sketch, "E82", {"start": v(-15, 108) * mm, "end": v(-15, 120) * mm});
            skLineSegment(sketch, "E83", {"start": v(33, 90) * mm, "end": v(15, 108) * mm});
            skLineSegment(sketch, "E84", {"start": v(15, 108) * mm, "end": v(15, 120) * mm});
            skArc(sketch, "E85", {"start": v(15, 120) * mm, "mid": v(0, 135) * mm, "end": v(-15, 120) * mm});
            skLineSegment(sketch, "E86", {"start": v(-80, 0) * mm, "end": v(80, 0) * mm, "construction": true});
            skLineSegment(sketch, "E87.MirrorCS", {"start": v(33, -90) * mm, "end": v(15, -108) * mm});
            skLineSegment(sketch, "E88.MirrorCS", {"start": v(15, -108) * mm, "end": v(15, -120) * mm});
            skArc(sketch, "E89.MirrorCS", {"start": v(15, -120) * mm, "mid": v(0, -135) * mm, "end": v(-15, -120) * mm});
            skLineSegment(sketch, "E90.MirrorCS", {"start": v(-15, -108) * mm, "end": v(-15, -120) * mm});
            skLineSegment(sketch, "E91.MirrorCS", {"start": v(-33, -90) * mm, "end": v(-15, -108) * mm});
            skCircle(sketch, "E92.MirrorC", {"center": v(0, -120) * mm, "radius": 6 * mm});
            skLineSegment(sketch, "E93.MirrorCS", {"start": v(0, -90) * mm, "end": v(0, -120) * mm, "construction": true});
            skSolve(sketch);
        }
        {
            var Q0;
            Q0=makeQuery(id+"F16.imprint","IMPRINT",FACE,{"disambiguationData":[TD([[makeQuery(id+"F16.imprint","IMPRINT",EDGE,{"derivedFrom":sQuery(id+"F16.wireOp",EDGE,"E80")}),-1.0]])]});
            var Q1;
            Q1=makeQuery(id+"F16.imprint","IMPRINT",FACE,{"disambiguationData":[TD([[makeQuery(id+"F16.imprint","IMPRINT",EDGE,{"derivedFrom":makeQuery(id+"F1.opExtrude","CAP_EDGE",EDGE,{"disambiguationData":[OSD([sQuery(id+"F0.wireOp",EDGE,"E1.left")])],"isStart":true})}),-1.0]])]});
            var Q2;
            {var subQ0=sQuery(id+"F16.wireOp",EDGE,"E87.MirrorCS");Q2=makeQuery(id+"F16.imprint","IMPRINT",FACE,{"disambiguationData":[TD([[makeQuery(id+"F16.imprint","IMPRINT",EDGE,{"derivedFrom":subQ0}),-1.0]])]});}
            var Q3;
            Q3=makeQuery(id+"F2.opExtrude","CAP_FACE",FACE,{"disambiguationData":[OSD([sQuery(id+"F0.wireOp",EDGE,"E12"),sQuery(id+"F0.wireOp",EDGE,"E13"),sQuery(id+"F0.wireOp",EDGE,"E14"),sQuery(id+"F0.wireOp",EDGE,"E15"),sQuery(id+"F0.wireOp",EDGE,"E17.filletArc"),sQuery(id+"F0.wireOp",EDGE,"E18.filletArc"),sQuery(id+"F0.wireOp",EDGE,"E19.filletArc"),sQuery(id+"F0.wireOp",EDGE,"E20.filletArc"),sQuery(id+"F0.wireOp",EDGE,"E25.0"),sQuery(id+"F0.wireOp",EDGE,"E25.1"),sQuery(id+"F0.wireOp",EDGE,"E25.2"),sQuery(id+"F0.wireOp",EDGE,"E25.3"),sQuery(id+"F0.wireOp",EDGE,"E25.4"),sQuery(id+"F0.wireOp",EDGE,"E25.5"),sQuery(id+"F0.wireOp",EDGE,"E25.6"),sQuery(id+"F0.wireOp",EDGE,"E25.7")])],"isStart":false});
            extrude(context, id + "F17", {"entities" : qUnion([Q0, Q1, Q2]), "endBound" : BoundingType.UP_TO_SURFACE, "endBoundEntityFace" : qUnion([Q3]), "depth" : 25 * mm});
        }
    });
